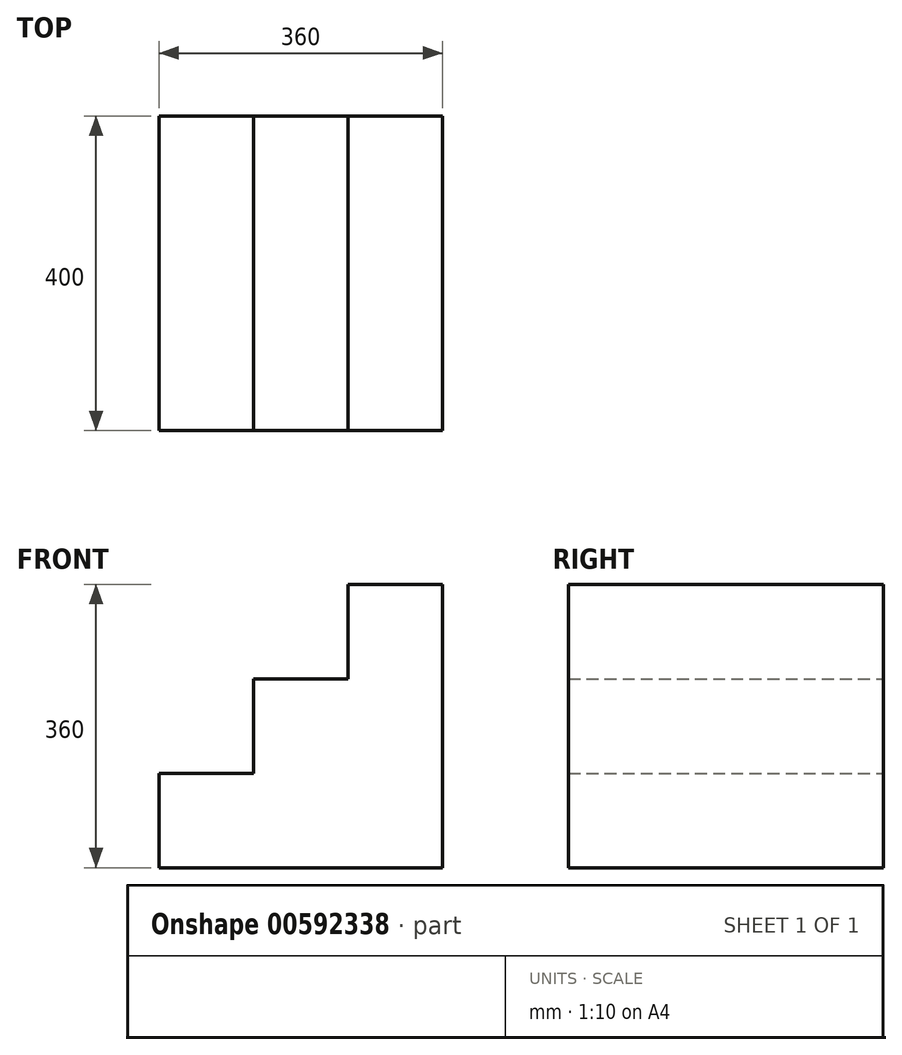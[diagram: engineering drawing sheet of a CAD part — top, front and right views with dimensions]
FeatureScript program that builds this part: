
annotation { "Feature Type Name" : "Feature", "Feature Type Description" : "" }
export const myFeature = defineFeature(function(context is Context, id is Id, definition is map)
    precondition{}
    {
        {
            var Q0;
            Q0=qCreatedBy(makeId("Front.planeOp"),FACE);
            var sketch = newSketch(context, id + "F0", { "sketchPlane" : qUnion([Q0])});
            skLineSegment(sketch, "E0", {"start": v(0, 0) * mm, "end": v(360, 0) * mm});
            skLineSegment(sketch, "E1", {"start": v(360, 0) * mm, "end": v(360, 360) * mm});
            skLineSegment(sketch, "E2", {"start": v(360, 360) * mm, "end": v(240, 360) * mm});
            skLineSegment(sketch, "E3", {"start": v(240, 240) * mm, "end": v(240, 360) * mm});
            skLineSegment(sketch, "E4", {"start": v(240, 240) * mm, "end": v(120, 240) * mm});
            skLineSegment(sketch, "E5", {"start": v(120, 120) * mm, "end": v(120, 240) * mm});
            skLineSegment(sketch, "E6", {"start": v(120, 120) * mm, "end": v(0, 120) * mm});
            skLineSegment(sketch, "E7", {"start": v(0, 120) * mm, "end": v(0, 0) * mm});
            skSolve(sketch);
        }
        {
            var Q0;
            Q0=makeQuery(id+"F0.imprint","IMPRINT",FACE,{"disambiguationData":[TD([[makeQuery(id+"F0.imprint","IMPRINT",EDGE,{"derivedFrom":sQuery(id+"F0.wireOp",EDGE,"E0")}),1.0]])]});
            extrude(context, id + "F1", {"entities" : qUnion([Q0]), "depth" : 400 * mm, "offsetDistance" : 25 * mm});
        }
    });
